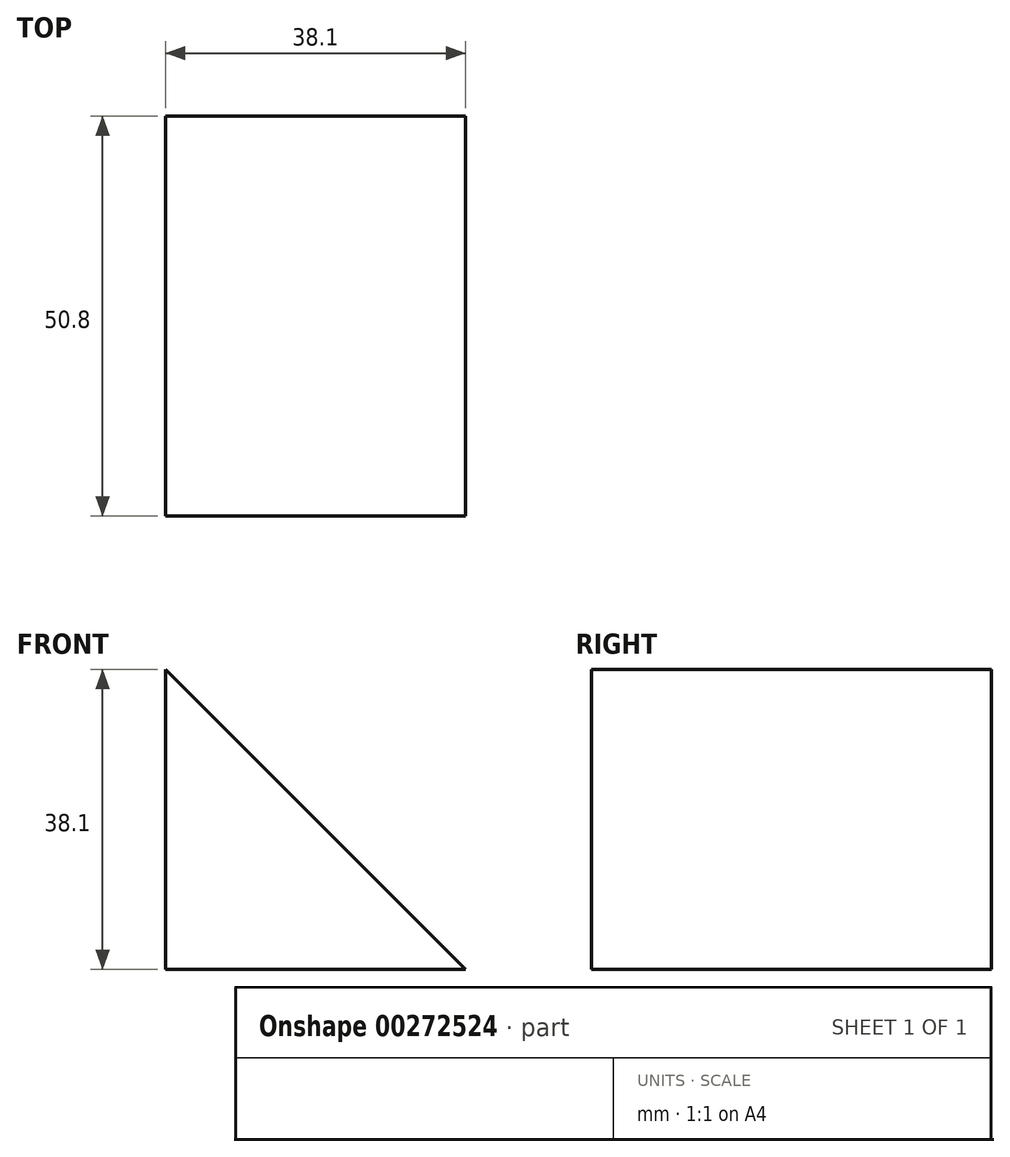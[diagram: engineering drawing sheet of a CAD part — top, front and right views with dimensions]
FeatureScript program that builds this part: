
annotation { "Feature Type Name" : "Feature", "Feature Type Description" : "" }
export const myFeature = defineFeature(function(context is Context, id is Id, definition is map)
    precondition{}
    {
        {
            var Q0;
            Q0=qCreatedBy(makeId("Front.planeOp"),FACE);
            var sketch = newSketch(context, id + "F0", { "sketchPlane" : qUnion([Q0])});
            skLineSegment(sketch, "E0.bottom", {"start": v(0, 0) * mm, "end": v(-38.1, 0) * mm});
            skLineSegment(sketch, "E0.right", {"start": v(-38.1, 0) * mm, "end": v(-38.1, 38.1) * mm});
            skLineSegment(sketch, "E1", {"start": v(-38.1, 38.1) * mm, "end": v(0, 0) * mm});
            skSolve(sketch);
        }
        {
            var Q0;
            Q0 = qSketchRegion(id + "F0", true);
            extrude(context, id + "F1", {"entities" : qUnion([Q0]), "depth" : 50.8 * mm});
        }
    });
